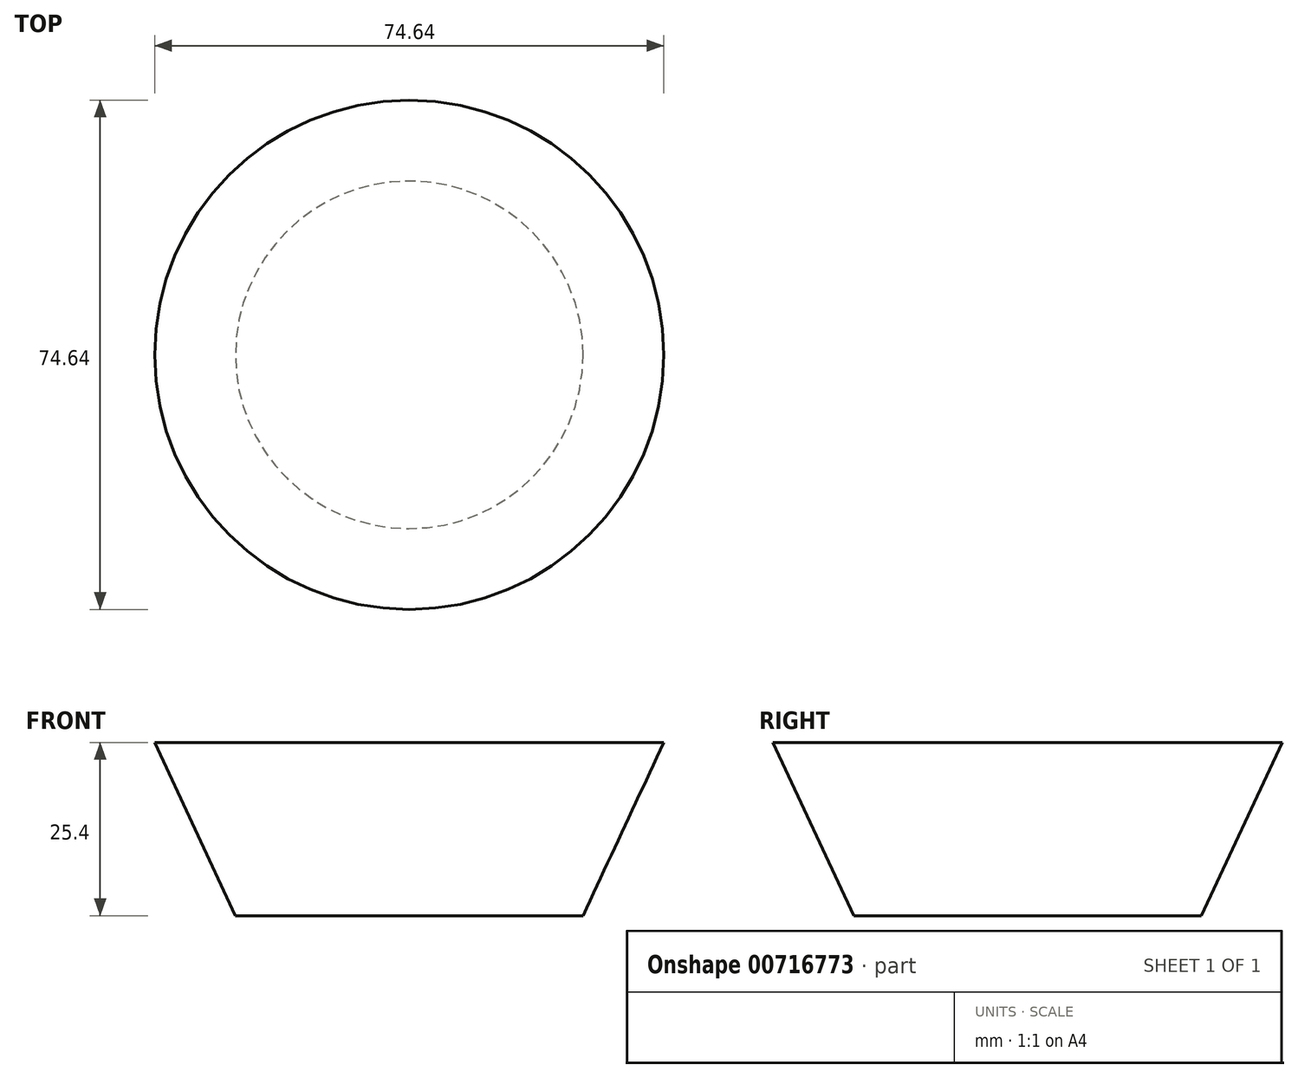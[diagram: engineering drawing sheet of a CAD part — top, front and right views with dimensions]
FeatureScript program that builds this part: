
annotation { "Feature Type Name" : "Feature", "Feature Type Description" : "" }
export const myFeature = defineFeature(function(context is Context, id is Id, definition is map)
    precondition{}
    {
        {
            var Q0;
            Q0=qCreatedBy(makeId("Top.planeOp"),FACE);
            var sketch = newSketch(context, id + "F0", { "sketchPlane" : qUnion([Q0])});
            skCircle(sketch, "E0", {"center": v(0, 0) * mm, "radius": 25.47 * mm});
            skSolve(sketch);
        }
        {
            var Q0;
            Q0 = qSketchRegion(id + "F0", true);
            extrude(context, id + "F1", {"entities" : qUnion([Q0]), "depth" : 25.4 * mm, "offsetDistance" : 25.4 * mm, "hasDraft" : true, "draftAngle" : 25 * degree});
        }
    });
